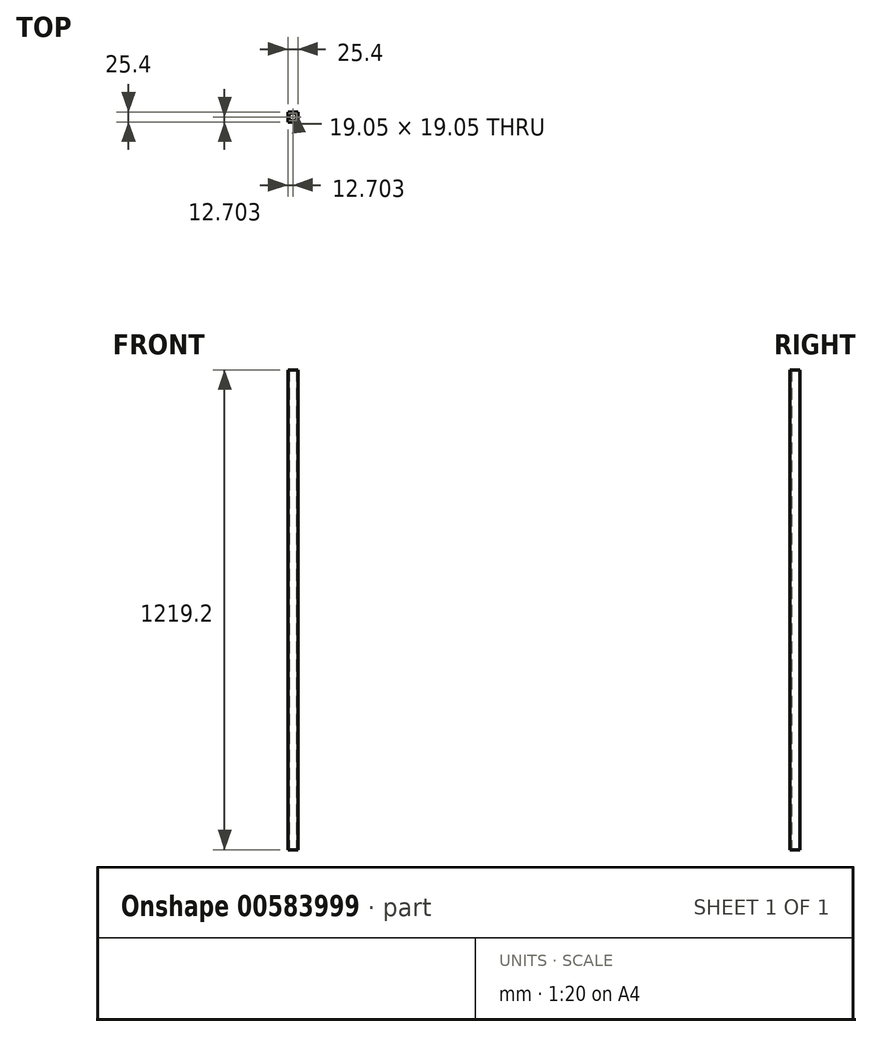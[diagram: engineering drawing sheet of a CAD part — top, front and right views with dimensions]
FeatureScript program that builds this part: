
annotation { "Feature Type Name" : "Feature", "Feature Type Description" : "" }
export const myFeature = defineFeature(function(context is Context, id is Id, definition is map)
    precondition{}
    {
        {
            var Q0;
            Q0=qCreatedBy(makeId("Top.planeOp"),FACE);
            var sketch = newSketch(context, id + "F0", { "sketchPlane" : qUnion([Q0])});
            skLineSegment(sketch, "E0.bottom", {"start": v(-6.57, 8.24) * mm, "end": v(12.48, 8.24) * mm});
            skLineSegment(sketch, "E0.top", {"start": v(-6.57, -10.81) * mm, "end": v(12.48, -10.81) * mm});
            skLineSegment(sketch, "E0.left", {"start": v(-6.57, 8.24) * mm, "end": v(-6.57, -10.81) * mm});
            skLineSegment(sketch, "E0.right", {"start": v(12.48, 8.24) * mm, "end": v(12.48, -10.81) * mm});
            skLineSegment(sketch, "E1.bottom", {"start": v(-9.75, 11.41) * mm, "end": v(15.65, 11.41) * mm});
            skLineSegment(sketch, "E1.top", {"start": v(-9.75, -13.99) * mm, "end": v(15.65, -13.99) * mm});
            skLineSegment(sketch, "E1.left", {"start": v(-9.75, 11.41) * mm, "end": v(-9.75, -13.99) * mm});
            skLineSegment(sketch, "E1.right", {"start": v(15.65, 11.41) * mm, "end": v(15.65, -13.99) * mm});
            skSolve(sketch);
        }
        {
            var Q0;
            Q0=makeQuery(id+"F0.imprint","IMPRINT",FACE,{"disambiguationData":[TD([[makeQuery(id+"F0.imprint","IMPRINT",EDGE,{"derivedFrom":sQuery(id+"F0.wireOp",EDGE,"E0.bottom")}),1.0]])]});
            extrude(context, id + "F1", {"entities" : qUnion([Q0]), "depth" : 1219.2 * mm, "offsetDistance" : 25.4 * mm});
        }
    });
